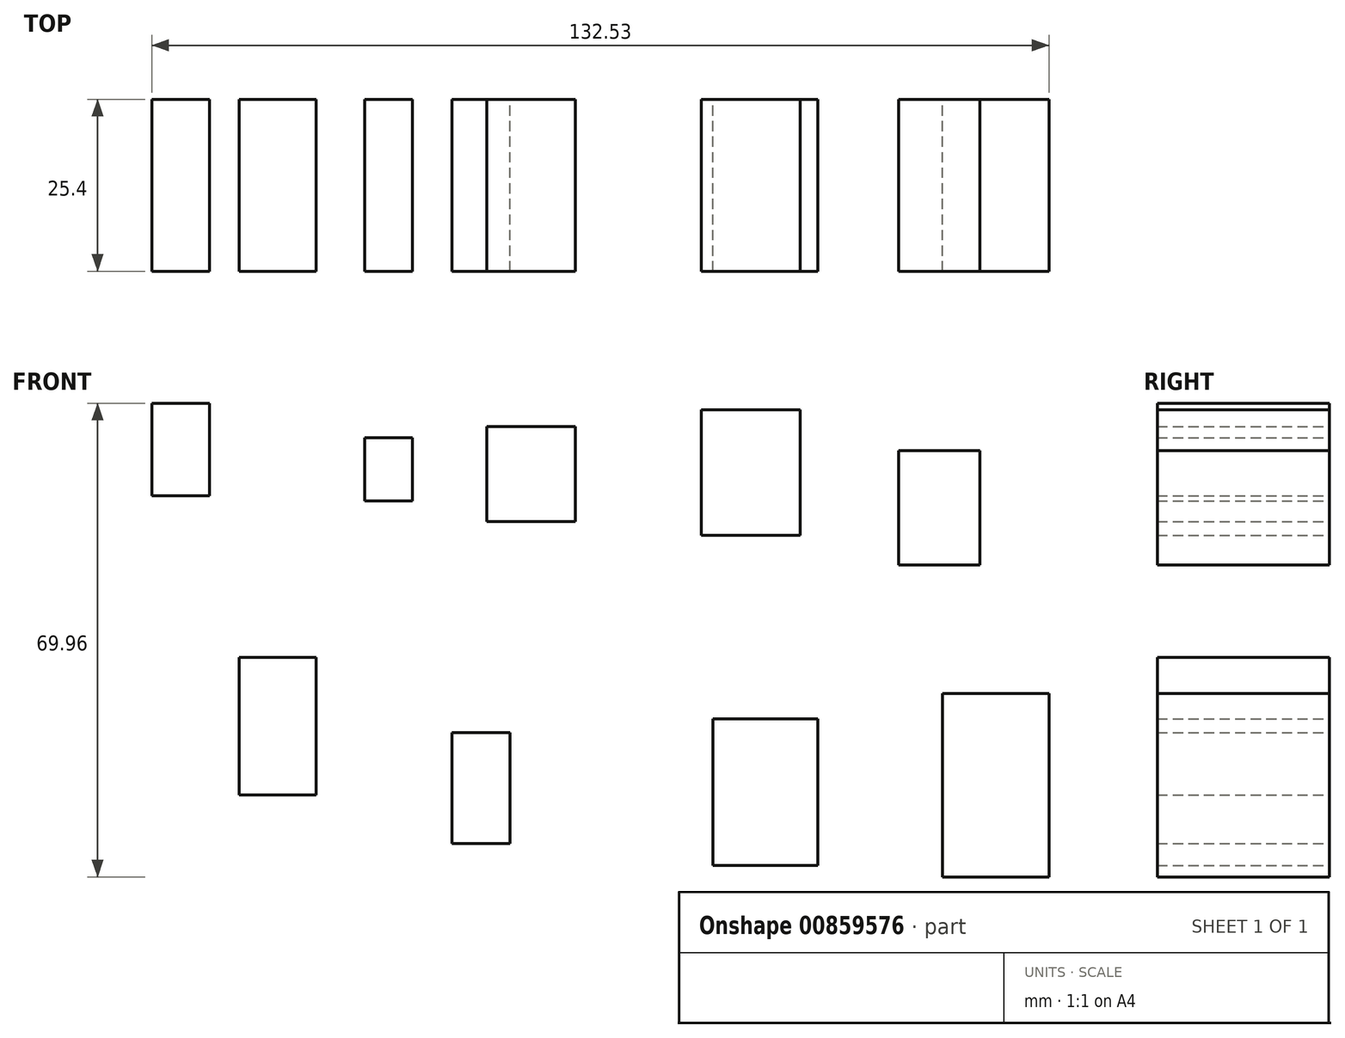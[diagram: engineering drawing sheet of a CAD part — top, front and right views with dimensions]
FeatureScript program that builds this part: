
annotation { "Feature Type Name" : "Feature", "Feature Type Description" : "" }
export const myFeature = defineFeature(function(context is Context, id is Id, definition is map)
    precondition{}
    {
        {
            var Q0;
            Q0=qCreatedBy(makeId("Front.planeOp"),FACE);
            var sketch = newSketch(context, id + "F0", { "sketchPlane" : qUnion([Q0])});
            skLineSegment(sketch, "E0.bottom", {"start": v(-60.96, 48.63) * mm, "end": v(-52.42, 48.63) * mm});
            skLineSegment(sketch, "E0.top", {"start": v(-60.96, 34.98) * mm, "end": v(-52.42, 34.98) * mm});
            skLineSegment(sketch, "E0.left", {"start": v(-60.96, 48.63) * mm, "end": v(-60.96, 34.98) * mm});
            skLineSegment(sketch, "E0.right", {"start": v(-52.42, 48.63) * mm, "end": v(-52.42, 34.98) * mm});
            skLineSegment(sketch, "E1.bottom", {"start": v(-29.48, 43.51) * mm, "end": v(-22.47, 43.51) * mm});
            skLineSegment(sketch, "E1.top", {"start": v(-29.48, 34.22) * mm, "end": v(-22.47, 34.22) * mm});
            skLineSegment(sketch, "E1.left", {"start": v(-29.48, 43.51) * mm, "end": v(-29.48, 34.22) * mm});
            skLineSegment(sketch, "E1.right", {"start": v(-22.47, 43.51) * mm, "end": v(-22.47, 34.22) * mm});
            skLineSegment(sketch, "E2.bottom", {"start": v(-11.47, 45.22) * mm, "end": v(1.61, 45.22) * mm});
            skLineSegment(sketch, "E2.top", {"start": v(-11.47, 31.19) * mm, "end": v(1.61, 31.19) * mm});
            skLineSegment(sketch, "E2.left", {"start": v(-11.47, 45.22) * mm, "end": v(-11.47, 31.19) * mm});
            skLineSegment(sketch, "E2.right", {"start": v(1.61, 45.22) * mm, "end": v(1.61, 31.19) * mm});
            skLineSegment(sketch, "E3.bottom", {"start": v(20.2, 47.68) * mm, "end": v(34.8, 47.68) * mm});
            skLineSegment(sketch, "E3.top", {"start": v(20.2, 29.1) * mm, "end": v(34.8, 29.1) * mm});
            skLineSegment(sketch, "E3.left", {"start": v(20.2, 47.68) * mm, "end": v(20.2, 29.1) * mm});
            skLineSegment(sketch, "E3.right", {"start": v(34.8, 47.68) * mm, "end": v(34.8, 29.1) * mm});
            skLineSegment(sketch, "E4.bottom", {"start": v(49.4, 41.62) * mm, "end": v(61.33, 41.62) * mm});
            skLineSegment(sketch, "E4.top", {"start": v(49.4, 24.74) * mm, "end": v(61.33, 24.74) * mm});
            skLineSegment(sketch, "E4.left", {"start": v(49.4, 41.62) * mm, "end": v(49.4, 24.74) * mm});
            skLineSegment(sketch, "E4.right", {"start": v(61.33, 41.62) * mm, "end": v(61.33, 24.74) * mm});
            skLineSegment(sketch, "E5.bottom", {"start": v(-48.06, 11.1) * mm, "end": v(-36.69, 11.1) * mm});
            skLineSegment(sketch, "E5.top", {"start": v(-48.06, -9.2) * mm, "end": v(-36.69, -9.2) * mm});
            skLineSegment(sketch, "E5.left", {"start": v(-48.06, 11.1) * mm, "end": v(-48.06, -9.2) * mm});
            skLineSegment(sketch, "E5.right", {"start": v(-36.69, 11.1) * mm, "end": v(-36.69, -9.2) * mm});
            skLineSegment(sketch, "E6.bottom", {"start": v(-16.59, 0) * mm, "end": v(-8.06, 0) * mm});
            skLineSegment(sketch, "E6.top", {"start": v(-16.59, -16.4) * mm, "end": v(-8.06, -16.4) * mm});
            skLineSegment(sketch, "E6.left", {"start": v(-16.59, 0) * mm, "end": v(-16.59, -16.4) * mm});
            skLineSegment(sketch, "E6.right", {"start": v(-8.06, 0) * mm, "end": v(-8.06, -16.4) * mm});
            skLineSegment(sketch, "E7.bottom", {"start": v(21.9, 2) * mm, "end": v(37.45, 2) * mm});
            skLineSegment(sketch, "E7.top", {"start": v(21.9, -19.62) * mm, "end": v(37.45, -19.62) * mm});
            skLineSegment(sketch, "E7.left", {"start": v(21.9, 2) * mm, "end": v(21.9, -19.62) * mm});
            skLineSegment(sketch, "E7.right", {"start": v(37.45, 2) * mm, "end": v(37.45, -19.62) * mm});
            skLineSegment(sketch, "E8.bottom", {"start": v(55.84, 5.78) * mm, "end": v(71.57, 5.78) * mm});
            skLineSegment(sketch, "E8.top", {"start": v(55.84, -21.33) * mm, "end": v(71.57, -21.33) * mm});
            skLineSegment(sketch, "E8.left", {"start": v(55.84, 5.78) * mm, "end": v(55.84, -21.33) * mm});
            skLineSegment(sketch, "E8.right", {"start": v(71.57, 5.78) * mm, "end": v(71.57, -21.33) * mm});
            skSolve(sketch);
        }
        {
            var Q0;
            Q0 = qSketchRegion(id + "F0", true);
            extrude(context, id + "F1", {"entities" : qUnion([Q0]), "depth" : 25.4 * mm, "offsetDistance" : 25.4 * mm});
        }
    });
